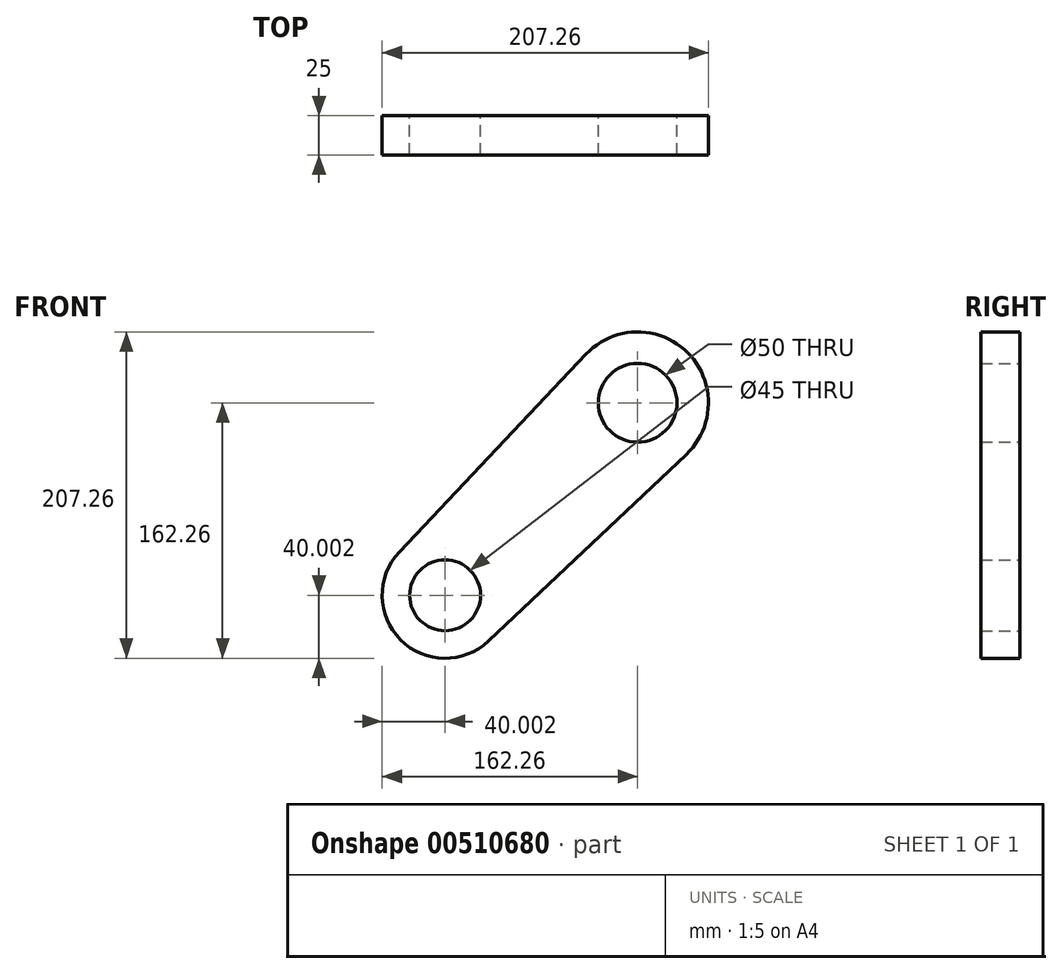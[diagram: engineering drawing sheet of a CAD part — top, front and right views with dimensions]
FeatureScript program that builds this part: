
annotation { "Feature Type Name" : "Feature", "Feature Type Description" : "" }
export const myFeature = defineFeature(function(context is Context, id is Id, definition is map)
    precondition{}
    {
        {
            var Q0;
            Q0=qCreatedBy(makeId("Front.planeOp"),FACE);
            var sketch = newSketch(context, id + "F0", { "sketchPlane" : qUnion([Q0])});
            skCircle(sketch, "E0", {"center": v(0, 0) * mm, "radius": 25 * mm});
            skCircle(sketch, "E1", {"center": v(0, 0) * mm, "radius": 45 * mm});
            skCircle(sketch, "E2", {"center": v(-122.26, -122.26) * mm, "radius": 22.5 * mm});
            skCircle(sketch, "E3", {"center": v(-122.26, -122.26) * mm, "radius": 40 * mm});
            skLineSegment(sketch, "E4", {"start": v(-151.35, -94.8) * mm, "end": v(-32.73, 30.89) * mm});
            skLineSegment(sketch, "E5", {"start": v(-94.8, -151.35) * mm, "end": v(30.89, -32.73) * mm});
            skLineSegment(sketch, "E6", {"start": v(-122.26, -122.26) * mm, "end": v(0, 0) * mm, "construction": true});
            skLineSegment(sketch, "E7", {"start": v(0, 0) * mm, "end": v(96.76, 0) * mm, "construction": true});
            skSolve(sketch);
        }
        {
            var Q0;
            Q0 = qSketchRegion(id + "F0", true);
            extrude(context, id + "F1", {"entities" : qUnion([Q0]), "depth" : 25 * mm, "offsetDistance" : 25 * mm});
        }
    });
